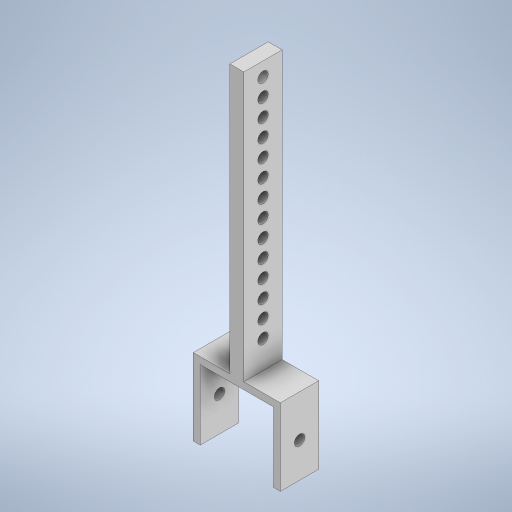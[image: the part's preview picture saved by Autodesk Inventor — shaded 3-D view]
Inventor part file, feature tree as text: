
AUTODESK INVENTOR PART (.ipt)
format: ipt  version: 2024 (Build 280153000, 153)  size: 309,760 bytes
history: native  units: mm
features: extrude x5, sketch x4, projected_geometry x2
ambient origin geometry x8: Origin, YZ Plane, XZ Plane, XY Plane, X Axis, Y Axis, Z Axis, Center Point
bodies: Body1 (feature_tree)
feature tree (11):
  extrude  "돌출3"  Depth=11.0mm
  sketch  "스케치5"
  extrude  "돌출4"  Depth=4.0mm
  extrude  "돌출5"  Depth=77.0mm TaperAngle=0.0deg
  extrude  "돌출6"  Depth=21.0mm
  extrude  "돌출7"  Depth=11.0mm
  sketch  "스케치4"
  sketch  "스케치6"
  projected_geometry  "투영된 루프1"
  sketch  "스케치7"
  projected_geometry  "투영된 루프2"
